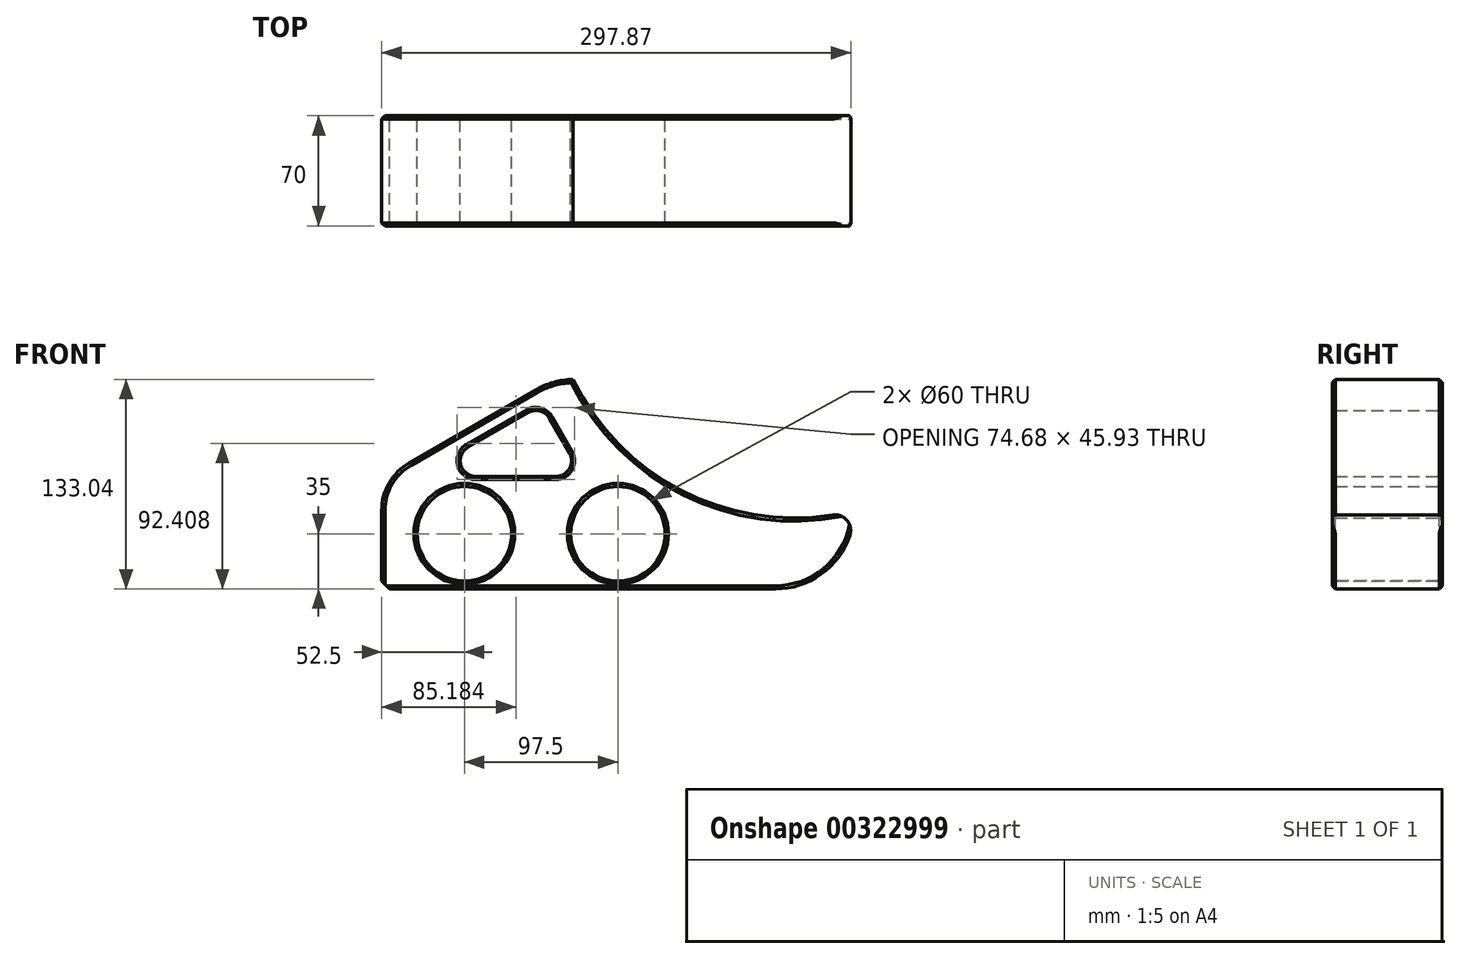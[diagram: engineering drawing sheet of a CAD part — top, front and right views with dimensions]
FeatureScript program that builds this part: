
annotation { "Feature Type Name" : "Feature", "Feature Type Description" : "" }
export const myFeature = defineFeature(function(context is Context, id is Id, definition is map)
    precondition{}
    {
        {
            var Q0;
            Q0=qCreatedBy(makeId("Front.planeOp"),FACE);
            var sketch = newSketch(context, id + "F0", { "sketchPlane" : qUnion([Q0])});
            skLineSegment(sketch, "E0", {"start": v(-157.76, 0) * mm, "end": v(158.79, 0) * mm, "construction": true});
            skLineSegment(sketch, "E1.bottom", {"start": v(150, -35) * mm, "end": v(-150, -35) * mm});
            skLineSegment(sketch, "E1.left", {"start": v(150, -35) * mm, "end": v(150, 14.8) * mm});
            skLineSegment(sketch, "E1.right", {"start": v(-150, -35) * mm, "end": v(-150, 14.8) * mm});
            skPoint(sketch, "E1.middle", {"position": v(0, 0) * mm});
            skCircle(sketch, "E2", {"center": v(0, 0) * mm, "radius": 30 * mm});
            skLineSegment(sketch, "E3", {"start": v(-132.5, 45.1) * mm, "end": v(-52.4, 91.35) * mm});
            skArc(sketch, "E4.filletArc", {"start": v(-132.5, 45.1) * mm, "mid": v(-145.31, 32.3) * mm, "end": v(-150, 14.8) * mm});
            skPoint(sketch, "E5.visualSharp", {"position": v(-41.9, 97.42) * mm});
            skArc(sketch, "E5.filletArc", {"start": v(-28.5, 98.04) * mm, "mid": v(-40.87, 96.2) * mm, "end": v(-52.4, 91.35) * mm});
            skLineSegment(sketch, "E6", {"start": v(0, 102.38) * mm, "end": v(0, -61.25) * mm, "construction": true});
            skLineSegment(sketch, "E7", {"start": v(0, 0) * mm, "end": v(-97.5, 0) * mm, "construction": true});
            skPoint(sketch, "E8", {"position": v(-97.5, 0) * mm});
            skCircle(sketch, "E9", {"center": v(-97.5, 0) * mm, "radius": 30 * mm});
            skLineSegment(sketch, "E10.0", {"start": v(-95.18, 55.1) * mm, "end": v(-57.15, 77.06) * mm});
            skLineSegment(sketch, "E11", {"start": v(-43.5, 73.4) * mm, "end": v(-30.82, 51.44) * mm});
            skLineSegment(sketch, "E12", {"start": v(-90.18, 36.44) * mm, "end": v(-39.48, 36.44) * mm});
            skPoint(sketch, "E13.visualSharp", {"position": v(-48.5, 82.06) * mm});
            skArc(sketch, "E13.filletArc", {"start": v(-43.5, 73.4) * mm, "mid": v(-49.57, 78.06) * mm, "end": v(-57.15, 77.06) * mm});
            skArc(sketch, "E14.filletArc", {"start": v(-39.48, 36.44) * mm, "mid": v(-30.82, 41.44) * mm, "end": v(-30.82, 51.44) * mm});
            skPoint(sketch, "E15.visualSharp", {"position": v(0, 38.68) * mm});
            skPoint(sketch, "E16.newPointA", {"position": v(48.5, 82.06) * mm});
            skPoint(sketch, "E17.visualSharp", {"position": v(-127.5, 36.44) * mm});
            skArc(sketch, "E17.filletArc", {"start": v(-95.18, 55.1) * mm, "mid": v(-99.84, 43.86) * mm, "end": v(-90.18, 36.44) * mm});
            skPoint(sketch, "E18.visualSharp", {"position": v(127.5, 36.44) * mm});
            skArc(sketch, "E19", {"start": v(-28.5, 98.04) * mm, "mid": v(45.97, 24.73) * mm, "end": v(150, 14.8) * mm});
            skSolve(sketch);
        }
        {
            var Q0;
            Q0=qSketchRegion(id+"F0",true);
            extrude(context, id + "F1", {"entities" : qUnion([Q0]), "depth" : 70 * mm, "symmetric" : true});
        }
        {
            var Q0;
            Q0=makeQuery(id+"F1.opExtrude","SWEPT_EDGE",EDGE,{"disambiguationData":[OSD([sQuery(id+"F0.wireOp",EDGE,"E1.bottom"),sQuery(id+"F0.wireOp",EDGE,"E1.left")])]});
            fillet(context, id + "F2", {"entities" : qUnion([Q0]), "radius" : 50 * mm, "tangentPropagation" : true, "allowEdgeOverflow" : false});
        }
        {
            var Q0;
            Q0=makeQuery(id+"F1.opExtrude","CAP_FACE",FACE,{"disambiguationData":[OSD([sQuery(id+"F0.wireOp",EDGE,"E1.bottom"),sQuery(id+"F0.wireOp",EDGE,"E1.left"),sQuery(id+"F0.wireOp",EDGE,"E1.right"),sQuery(id+"F0.wireOp",EDGE,"E2"),sQuery(id+"F0.wireOp",EDGE,"E3"),sQuery(id+"F0.wireOp",EDGE,"E4.filletArc"),sQuery(id+"F0.wireOp",EDGE,"E5.filletArc"),sQuery(id+"F0.wireOp",EDGE,"2128d712-c22e-43d0-b137-ae846bd3470c0.MirrorCS"),sQuery(id+"F0.wireOp",EDGE,"ead384d1-ae69-4692-b830-1a13f9f5a69b0.MirrorCS"),sQuery(id+"F0.wireOp",EDGE,"37f9a7ff-8684-4468-8a72-e05079eaa0670.MirrorCS"),sQuery(id+"F0.wireOp",EDGE,"Lrirhn2S-7brx-2jdC-clf1-sQWSoA0U2pV4"),sQuery(id+"F0.wireOp",EDGE,"E9"),sQuery(id+"F0.wireOp",EDGE,"E10.0"),sQuery(id+"F0.wireOp",EDGE,"fc2dcb0f-4b4e-4361-bf83-8e2945b27883.0"),sQuery(id+"F0.wireOp",EDGE,"da70da69-e66b-4109-82d2-453cd6daba01.0"),sQuery(id+"F0.wireOp",EDGE,"AouGleSv-KkGm-sB8C-ZEsv-O4xofjI2ggc6"),sQuery(id+"F0.wireOp",EDGE,"E11"),sQuery(id+"F0.wireOp",EDGE,"E12"),sQuery(id+"F0.wireOp",EDGE,"ibZBRqrK-dixR-fJSc-eGvf-ZQZpcMRPZl58"),sQuery(id+"F0.wireOp",EDGE,"4ea5772b-329a-4e50-88f7-68c20ca4a20b0.MirrorCS"),sQuery(id+"F0.wireOp",EDGE,"01e6399d-9f67-49b3-929a-f7497086e1730.MirrorCS"),sQuery(id+"F0.wireOp",EDGE,"E13.filletArc"),sQuery(id+"F0.wireOp",EDGE,"E14.filletArc"),sQuery(id+"F0.wireOp",EDGE,"E15.filletArc"),sQuery(id+"F0.wireOp",EDGE,"7a9b99ec-dd7e-44b2-9577-c392ffdbf900.filletArc"),sQuery(id+"F0.wireOp",EDGE,"3fdbf697-db4c-413a-9f31-464b24b49e91.filletArc"),sQuery(id+"F0.wireOp",EDGE,"E16.filletArc"),sQuery(id+"F0.wireOp",EDGE,"00bd977d-d024-4b05-abdb-e15cf0350885.filletArc"),sQuery(id+"F0.wireOp",EDGE,"E17.filletArc"),sQuery(id+"F0.wireOp",EDGE,"E18.filletArc")])],"isStart":false});
            var Q1;
            Q1=makeQuery(id+"F1.opExtrude","CAP_FACE",FACE,{"disambiguationData":[OSD([sQuery(id+"F0.wireOp",EDGE,"E1.bottom"),sQuery(id+"F0.wireOp",EDGE,"E1.left"),sQuery(id+"F0.wireOp",EDGE,"E1.right"),sQuery(id+"F0.wireOp",EDGE,"E2"),sQuery(id+"F0.wireOp",EDGE,"E3"),sQuery(id+"F0.wireOp",EDGE,"E4.filletArc"),sQuery(id+"F0.wireOp",EDGE,"E5.filletArc"),sQuery(id+"F0.wireOp",EDGE,"2128d712-c22e-43d0-b137-ae846bd3470c0.MirrorCS"),sQuery(id+"F0.wireOp",EDGE,"ead384d1-ae69-4692-b830-1a13f9f5a69b0.MirrorCS"),sQuery(id+"F0.wireOp",EDGE,"37f9a7ff-8684-4468-8a72-e05079eaa0670.MirrorCS"),sQuery(id+"F0.wireOp",EDGE,"Lrirhn2S-7brx-2jdC-clf1-sQWSoA0U2pV4"),sQuery(id+"F0.wireOp",EDGE,"E9"),sQuery(id+"F0.wireOp",EDGE,"E10.0"),sQuery(id+"F0.wireOp",EDGE,"fc2dcb0f-4b4e-4361-bf83-8e2945b27883.0"),sQuery(id+"F0.wireOp",EDGE,"da70da69-e66b-4109-82d2-453cd6daba01.0"),sQuery(id+"F0.wireOp",EDGE,"AouGleSv-KkGm-sB8C-ZEsv-O4xofjI2ggc6"),sQuery(id+"F0.wireOp",EDGE,"E11"),sQuery(id+"F0.wireOp",EDGE,"E12"),sQuery(id+"F0.wireOp",EDGE,"ibZBRqrK-dixR-fJSc-eGvf-ZQZpcMRPZl58"),sQuery(id+"F0.wireOp",EDGE,"4ea5772b-329a-4e50-88f7-68c20ca4a20b0.MirrorCS"),sQuery(id+"F0.wireOp",EDGE,"01e6399d-9f67-49b3-929a-f7497086e1730.MirrorCS"),sQuery(id+"F0.wireOp",EDGE,"E13.filletArc"),sQuery(id+"F0.wireOp",EDGE,"E14.filletArc"),sQuery(id+"F0.wireOp",EDGE,"E15.filletArc"),sQuery(id+"F0.wireOp",EDGE,"7a9b99ec-dd7e-44b2-9577-c392ffdbf900.filletArc"),sQuery(id+"F0.wireOp",EDGE,"3fdbf697-db4c-413a-9f31-464b24b49e91.filletArc"),sQuery(id+"F0.wireOp",EDGE,"E16.filletArc"),sQuery(id+"F0.wireOp",EDGE,"00bd977d-d024-4b05-abdb-e15cf0350885.filletArc"),sQuery(id+"F0.wireOp",EDGE,"E17.filletArc"),sQuery(id+"F0.wireOp",EDGE,"E18.filletArc")])],"isStart":true});
            chamfer(context, id + "F3", {"entities" : qUnion([Q0, Q1]), "width" : 2 * mm, "tangentPropagation" : true});
        }
        {
            var Q0;
            Q0=makeQuery(id+"F1.opExtrude","SWEPT_EDGE",EDGE,{"disambiguationData":[OSD([sQuery(id+"F0.wireOp",EDGE,"E1.bottom"),sQuery(id+"F0.wireOp",EDGE,"E1.right")])]});
            chamfer(context, id + "F4", {"entities" : qUnion([Q0]), "width" : 5 * mm, "tangentPropagation" : true});
        }
        {
            var Q0;
            Q0=makeQuery(id+"F2.opFillet","BLEND_EDGE",EDGE,{"blendedFrom":[makeQuery(id+"F1.opExtrude","SWEPT_EDGE",EDGE,{"disambiguationData":[OSD([sQuery(id+"F0.wireOp",EDGE,"E1.bottom"),sQuery(id+"F0.wireOp",EDGE,"E1.left")])]}),makeQuery(id+"F1.opExtrude","SWEPT_FACE",FACE,{"disambiguationData":[OSD([sQuery(id+"F0.wireOp",EDGE,"E19")])]})],"blendedInto":[makeQuery(id+"F1.opExtrude","SWEPT_FACE",FACE,{"disambiguationData":[OSD([sQuery(id+"F0.wireOp",EDGE,"E19")])]})]});
            fillet(context, id + "F5", {"entities" : qUnion([Q0]), "radius" : 10 * mm, "tangentPropagation" : true, "allowEdgeOverflow" : false});
        }
    });
